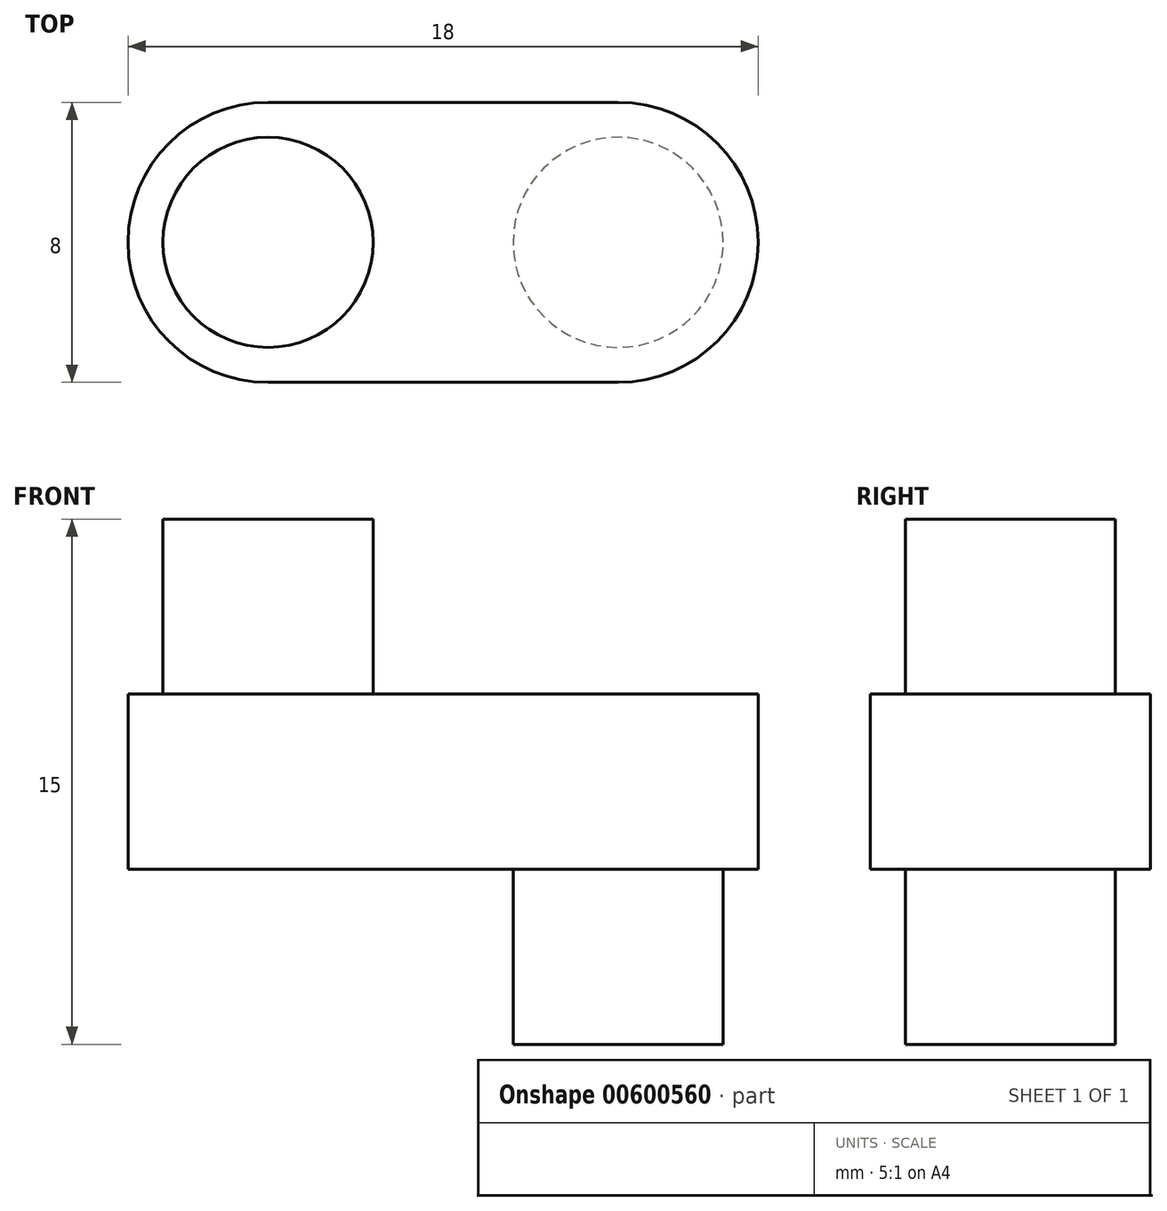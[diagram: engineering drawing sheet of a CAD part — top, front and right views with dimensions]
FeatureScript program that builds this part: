
annotation { "Feature Type Name" : "Feature", "Feature Type Description" : "" }
export const myFeature = defineFeature(function(context is Context, id is Id, definition is map)
    precondition{}
    {
        {
            var Q0;
            Q0=qCreatedBy(makeId("Top.planeOp"),FACE);
            var sketch = newSketch(context, id + "F0", { "sketchPlane" : qUnion([Q0])});
            skLineSegment(sketch, "E0", {"start": v(0, 0) * mm, "end": v(10, 0) * mm, "construction": true});
            skArc(sketch, "E1.0.startCap", {"start": v(0, -4) * mm, "mid": v(-4, 0) * mm, "end": v(0, 4) * mm});
            skArc(sketch, "E1.0.endCap", {"start": v(10, 4) * mm, "mid": v(14, 0) * mm, "end": v(10, -4) * mm});
            skLineSegment(sketch, "E1.0.left", {"start": v(0, 4) * mm, "end": v(10, 4) * mm});
            skLineSegment(sketch, "E1.0.right", {"start": v(0, -4) * mm, "end": v(10, -4) * mm});
            skSolve(sketch);
        }
        {
            var Q0;
            Q0 = qSketchRegion(id + "F0", true);
            extrude(context, id + "F1", {"entities" : qUnion([Q0]), "depth" : 5 * mm, "offsetDistance" : 25 * mm});
        }
        {
            var Q0;
            Q0=makeQuery(id+"F1.opExtrude","CAP_FACE",FACE,{"disambiguationData":[OSD([sQuery(id+"F0.wireOp",EDGE,"E1.0.startCap"),sQuery(id+"F0.wireOp",EDGE,"E1.0.endCap"),sQuery(id+"F0.wireOp",EDGE,"E1.0.left"),sQuery(id+"F0.wireOp",EDGE,"E1.0.right")])],"isStart":false});
            var sketch = newSketch(context, id + "F2", { "sketchPlane" : qUnion([Q0])});
            skCircle(sketch, "E2", {"center": v(0, 0) * mm, "radius": 3 * mm});
            skSolve(sketch);
        }
        {
            var Q0;
            Q0 = qSketchRegion(id + "F2", true);
            extrude(context, id + "F3", {"entities" : qUnion([Q0]), "operationType" : NewBodyOperationType.ADD, "depth" : 5 * mm, "offsetDistance" : 25 * mm});
        }
        {
            var Q0;
            Q0=makeQuery(id+"F1.opExtrude","CAP_FACE",FACE,{"disambiguationData":[OSD([sQuery(id+"F0.wireOp",EDGE,"E1.0.startCap"),sQuery(id+"F0.wireOp",EDGE,"E1.0.endCap"),sQuery(id+"F0.wireOp",EDGE,"E1.0.left"),sQuery(id+"F0.wireOp",EDGE,"E1.0.right")])],"isStart":true});
            var sketch = newSketch(context, id + "F4", { "sketchPlane" : qUnion([Q0])});
            skCircle(sketch, "E3", {"center": v(10, 0) * mm, "radius": 3 * mm});
            skSolve(sketch);
        }
        {
            var Q0;
            Q0 = qSketchRegion(id + "F4", true);
            extrude(context, id + "F5", {"entities" : qUnion([Q0]), "operationType" : NewBodyOperationType.ADD, "depth" : 5 * mm, "offsetDistance" : 25 * mm});
        }
    });
